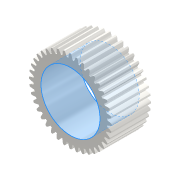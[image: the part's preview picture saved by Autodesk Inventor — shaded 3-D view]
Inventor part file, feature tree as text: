
AUTODESK INVENTOR PART (.ipt)
format: ipt  version: 2020.3 (Build 243373010, 373A)  size: 356,352 bytes
history: native  units: mm (DEFAULTED — no unit token found)
features: plane x3, other x3, sketch x3, extrude x2
ambient origin geometry x8: Origin, YZ Plane, XZ Plane, XY Plane, X Axis, Y Axis, Z Axis, Center Point
bodies: Solid1 (feature_tree)
feature tree (11):
  extrude  "Extrusion1"  Depth=10.0mm TaperAngle=0.0deg
  plane  "Work Plane2"
  plane  "Work Plane8"
  plane  "Work Plane9"
  other  "Spur Gear"
  extrude  "Extrusion2"  Depth=10.0mm TaperAngle=0.0deg
  sketch  "Sketch1"  dims[d0=21.0mm d1=10.0mm d2=0.0mm]
  sketch  "Sketch2"  dims[d3=20.0mm d4=10.0mm d5=0.0mm]
  other  "Srf1"
  sketch  "Sketch3"  dims[d16=15.0mm d17=0.0mm d34=0.785398mm d39=0.0mm d41=0.0mm d43=15.0mm d46=15.0mm d47=0.0mm d48=0.0mm d49=15.0mm d50=0.0mm d51=0.0mm]
  other  "Pitch Diameter"
